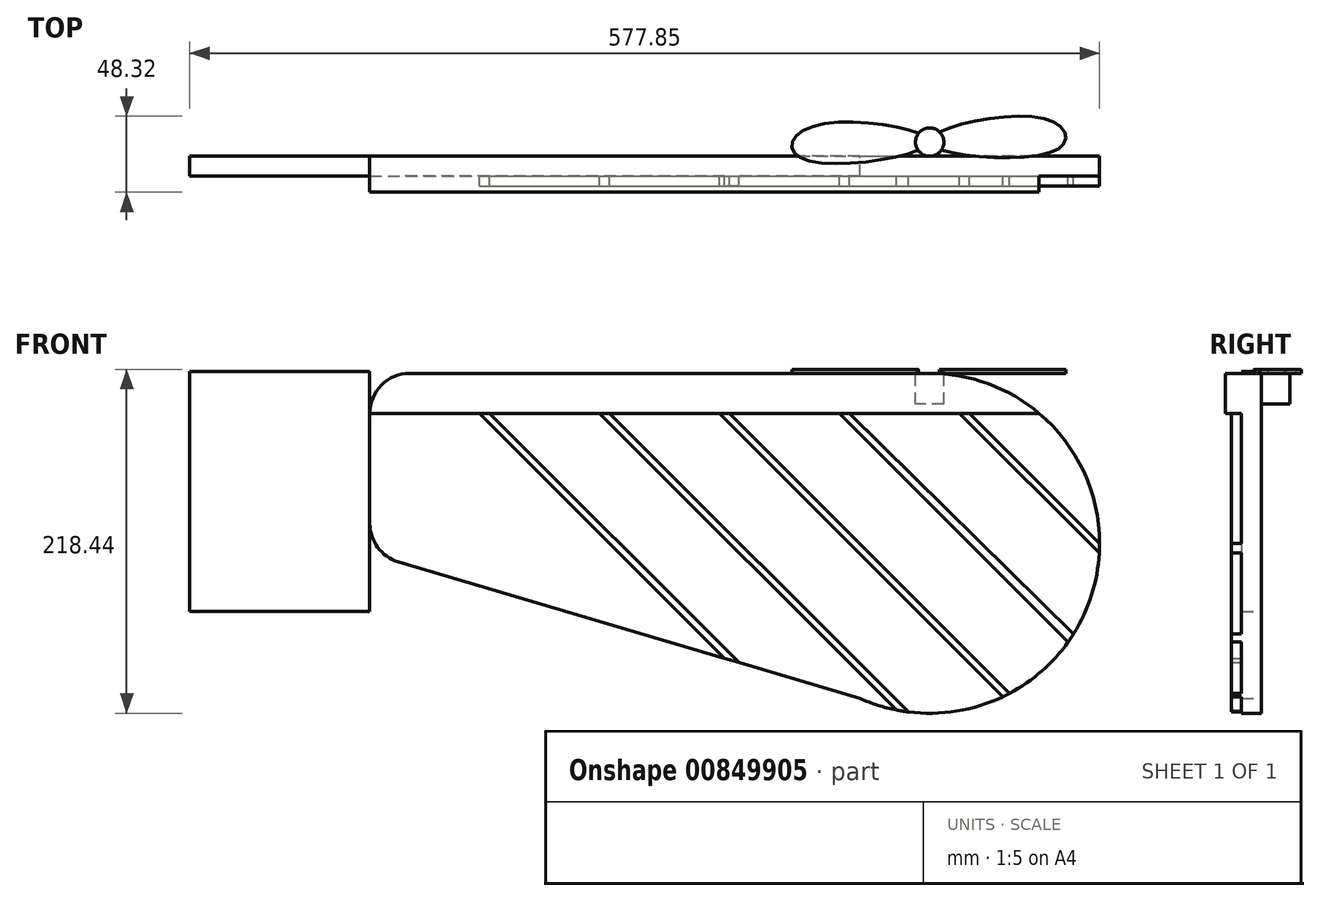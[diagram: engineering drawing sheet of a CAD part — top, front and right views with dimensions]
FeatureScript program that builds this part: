
annotation { "Feature Type Name" : "Feature", "Feature Type Description" : "" }
export const myFeature = defineFeature(function(context is Context, id is Id, definition is map)
    precondition{}
    {
        {
            var Q0;
            Q0=qCreatedBy(makeId("Front.planeOp"),FACE);
            var sketch = newSketch(context, id + "F0", { "sketchPlane" : qUnion([Q0])});
            skLineSegment(sketch, "E0", {"start": v(0, 18.97) * mm, "end": v(0, 88.9) * mm});
            skLineSegment(sketch, "E1", {"start": v(25.4, 114.3) * mm, "end": v(355.6, 114.3) * mm});
            skLineSegment(sketch, "E2", {"start": v(311.37, -92.12) * mm, "end": v(18.2, -5.38) * mm});
            skArc(sketch, "E3", {"start": v(311.37, -92.12) * mm, "mid": v(461.15, -16.27) * mm, "end": v(355.6, 114.3) * mm});
            skPoint(sketch, "E4.visualSharp", {"position": v(0, 114.3) * mm});
            skArc(sketch, "E4.filletArc", {"start": v(25.4, 114.3) * mm, "mid": v(7.44, 106.86) * mm, "end": v(0, 88.9) * mm});
            skPoint(sketch, "E5.visualSharp", {"position": v(0, 0) * mm});
            skArc(sketch, "E5.filletArc", {"start": v(0, 18.97) * mm, "mid": v(5.05, 3.77) * mm, "end": v(18.2, -5.38) * mm});
            skSolve(sketch);
        }
        {
            var Q0;
            Q0=makeQuery(id+"F0.imprint","IMPRINT",FACE,{"disambiguationData":[TD([[makeQuery(id+"F0.imprint","IMPRINT",EDGE,{"derivedFrom":sQuery(id+"F0.wireOp",EDGE,"E0")}),-1.0]])]});
            extrude(context, id + "F1", {"entities" : qUnion([Q0]), "depth" : 12.7 * mm, "offsetDistance" : 25.4 * mm});
        }
        {
            var Q0;
            Q0=makeQuery(id+"F1.opExtrude","CAP_FACE",FACE,{"disambiguationData":[OSD([sQuery(id+"F0.wireOp",EDGE,"E0"),sQuery(id+"F0.wireOp",EDGE,"E1"),sQuery(id+"F0.wireOp",EDGE,"E2"),sQuery(id+"F0.wireOp",EDGE,"E3"),sQuery(id+"F0.wireOp",EDGE,"E4.filletArc"),sQuery(id+"F0.wireOp",EDGE,"E5.filletArc")])],"isStart":false});
            var sketch = newSketch(context, id + "F2", { "sketchPlane" : qUnion([Q0])});
            skLineSegment(sketch, "E6", {"start": v(0, 88.9) * mm, "end": v(425.16, 88.9) * mm});
            skSolve(sketch);
        }
        {
            var Q0;
            {var subQ0=sQuery(id+"F2.wireOp",EDGE,"E6");Q0=makeQuery(id+"F2.imprint","IMPRINT",FACE,{"disambiguationData":[TD([[makeQuery(id+"F2.imprint","IMPRINT",EDGE,{"derivedFrom":subQ0}),1.0]])]});}
            extrude(context, id + "F3", {"entities" : qUnion([Q0]), "operationType" : NewBodyOperationType.ADD, "depth" : 10.16 * mm, "offsetDistance" : 25.4 * mm});
        }
        {
            var Q0;
            Q0=makeQuery(id+"F1.opExtrude","CAP_FACE",FACE,{"disambiguationData":[OSD([sQuery(id+"F0.wireOp",EDGE,"E0"),sQuery(id+"F0.wireOp",EDGE,"E1"),sQuery(id+"F0.wireOp",EDGE,"E2"),sQuery(id+"F0.wireOp",EDGE,"E3"),sQuery(id+"F0.wireOp",EDGE,"E4.filletArc"),sQuery(id+"F0.wireOp",EDGE,"E5.filletArc")])],"isStart":false});
            var sketch = newSketch(context, id + "F4", { "sketchPlane" : qUnion([Q0])});
            skPoint(sketch, "E7", {"position": v(0, 88.9) * mm});
            skPoint(sketch, "E8", {"position": v(69.85, 88.9) * mm});
            skPoint(sketch, "E9", {"position": v(76.2, 88.9) * mm});
            skPoint(sketch, "E10", {"position": v(146.05, 88.9) * mm});
            skPoint(sketch, "E11", {"position": v(152.4, 88.9) * mm});
            skPoint(sketch, "E12", {"position": v(222.25, 88.9) * mm});
            skPoint(sketch, "E13", {"position": v(228.6, 88.9) * mm});
            skPoint(sketch, "E14", {"position": v(298.45, 88.9) * mm});
            skPoint(sketch, "E15", {"position": v(304.8, 88.9) * mm});
            skPoint(sketch, "E16", {"position": v(374.65, 88.9) * mm});
            skPoint(sketch, "E17", {"position": v(381, 88.9) * mm});
            skLineSegment(sketch, "E18", {"start": v(69.85, 88.9) * mm, "end": v(225.45, -66.7) * mm});
            skLineSegment(sketch, "E19", {"start": v(76.2, 88.9) * mm, "end": v(234.47, -69.37) * mm});
            skLineSegment(sketch, "E20", {"start": v(146.05, 88.9) * mm, "end": v(334.46, -99.5) * mm});
            skLineSegment(sketch, "E21", {"start": v(152.4, 88.9) * mm, "end": v(342.05, -100.75) * mm});
            skLineSegment(sketch, "E22", {"start": v(222.25, 88.9) * mm, "end": v(402.18, -91.03) * mm});
            skLineSegment(sketch, "E23", {"start": v(228.6, 88.9) * mm, "end": v(408.53, -91.03) * mm});
            skLineSegment(sketch, "E24", {"start": v(298.45, 88.9) * mm, "end": v(443.57, -56.22) * mm});
            skLineSegment(sketch, "E25", {"start": v(304.8, 88.9) * mm, "end": v(447, -51.1) * mm});
            skLineSegment(sketch, "E26", {"start": v(374.65, 88.9) * mm, "end": v(463.37, 0.18) * mm});
            skLineSegment(sketch, "E27", {"start": v(381, 88.9) * mm, "end": v(463.55, 6.35) * mm});
            skLineSegment(sketch, "E28", {"start": v(69.85, 88.9) * mm, "end": v(76.2, 88.9) * mm});
            skLineSegment(sketch, "E29", {"start": v(225.45, -66.7) * mm, "end": v(234.47, -69.37) * mm});
            skSolve(sketch);
        }
        {
            var Q0;
            Q0=makeQuery(id+"F4.imprint","IMPRINT",FACE,{"disambiguationData":[TD([[makeQuery(id+"F4.imprint","IMPRINT",EDGE,{"derivedFrom":sQuery(id+"F4.wireOp",EDGE,"E18")}),1.0]])]});
            var Q1;
            {var subQ0=sQuery(id+"F4.wireOp",EDGE,"E20");Q1=makeQuery(id+"F4.imprint","IMPRINT",FACE,{"disambiguationData":[TD([[makeQuery(id+"F4.imprint","IMPRINT",EDGE,{"derivedFrom":subQ0}),1.0]])]});}
            var Q2;
            {var subQ0=sQuery(id+"F4.wireOp",EDGE,"E22");Q2=makeQuery(id+"F4.imprint","IMPRINT",FACE,{"disambiguationData":[TD([[makeQuery(id+"F4.imprint","IMPRINT",EDGE,{"derivedFrom":subQ0}),1.0]])]});}
            var Q3;
            {var subQ0=sQuery(id+"F4.wireOp",EDGE,"E24");Q3=makeQuery(id+"F4.imprint","IMPRINT",FACE,{"disambiguationData":[TD([[makeQuery(id+"F4.imprint","IMPRINT",EDGE,{"derivedFrom":subQ0}),1.0]])]});}
            var Q4;
            {var subQ0=sQuery(id+"F4.wireOp",EDGE,"E26");Q4=makeQuery(id+"F4.imprint","IMPRINT",FACE,{"disambiguationData":[TD([[makeQuery(id+"F4.imprint","IMPRINT",EDGE,{"derivedFrom":subQ0}),1.0]])]});}
            extrude(context, id + "F5", {"entities" : qUnion([Q0, Q1, Q2, Q3, Q4]), "operationType" : NewBodyOperationType.ADD, "depth" : 6.35 * mm, "offsetDistance" : 25.4 * mm});
        }
        {
            var Q0;
            Q0=makeQuery(id+"F1.opExtrude","SWEPT_BODY",BODY,{"disambiguationData":[OSD([sQuery(id+"F0.wireOp",EDGE,"E0"),sQuery(id+"F0.wireOp",EDGE,"E1"),sQuery(id+"F0.wireOp",EDGE,"E2"),sQuery(id+"F0.wireOp",EDGE,"E3"),sQuery(id+"F0.wireOp",EDGE,"E4.filletArc"),sQuery(id+"F0.wireOp",EDGE,"E5.filletArc")])]});
            transform(context, id + "F6", {"entities" : qUnion([Q0]), "transformType" : TransformType.TRANSLATION_3D, "dx" : 0 * mm, "dy" : 0 * mm, "dz" : 0 * mm, "makeCopy" : true});
        }
        {
            var Q0;
            Q0=qCreatedBy(makeId("Front.planeOp"),FACE);
            var sketch = newSketch(context, id + "F7", { "sketchPlane" : qUnion([Q0])});
            skLineSegment(sketch, "E30.bottom", {"start": v(0, -36.94) * mm, "end": v(-114.3, -36.94) * mm});
            skLineSegment(sketch, "E30.top", {"start": v(0, 115.46) * mm, "end": v(-114.3, 115.46) * mm});
            skLineSegment(sketch, "E30.left", {"start": v(0, -36.94) * mm, "end": v(0, 115.46) * mm});
            skLineSegment(sketch, "E30.right", {"start": v(-114.3, -36.94) * mm, "end": v(-114.3, 115.46) * mm});
            skSolve(sketch);
        }
        {
            var Q0;
            Q0=makeQuery(id+"F7.imprint","IMPRINT",FACE,{"disambiguationData":[TD([[makeQuery(id+"F7.imprint","IMPRINT",EDGE,{"derivedFrom":sQuery(id+"F7.wireOp",EDGE,"E30.bottom")}),-1.0]])]});
            extrude(context, id + "F8", {"entities" : qUnion([Q0]), "depth" : 12.7 * mm, "offsetDistance" : 25.4 * mm});
        }
        {
            var Q0;
            {var subQ0=sQuery(id+"F0.wireOp",EDGE,"E1");Q0=makeQuery(id+"F3.boolean.opBoolean","MERGE",FACE,{"derivedFrom":[makeQuery(id+"F1.opExtrude","SWEPT_FACE",FACE,{"disambiguationData":[OSD([subQ0])]}),makeQuery(id+"F3.opExtrude","SWEPT_FACE",FACE,{"disambiguationData":[OSD([subQ0])]})]});}
            var sketch = newSketch(context, id + "F9", { "sketchPlane" : qUnion([Q0])});
            skCircle(sketch, "E31", {"center": v(355.63, 9.02) * mm, "radius": 9.02 * mm});
            skPoint(sketch, "E31.first.point", {"position": v(355.6, 0) * mm});
            skPoint(sketch, "E31.second.point", {"position": v(355.6, 18.03) * mm});
            skPoint(sketch, "E31.third.point", {"position": v(346.75, 7.48) * mm});
            skSolve(sketch);
        }
        {
            var Q0;
            Q0=makeQuery(id+"F9.imprint","IMPRINT",FACE,{"disambiguationData":[TD([[makeQuery(id+"F9.imprint","IMPRINT",EDGE,{"derivedFrom":sQuery(id+"F9.wireOp",EDGE,"E31")}),1.0]])]});
            extrude(context, id + "F10", {"entities" : qUnion([Q0]), "oppositeDirection" : true, "depth" : 19.56 * mm, "offsetDistance" : 25.4 * mm});
        }
        {
            var Q0;
            Q0=makeQuery(id+"F10.opExtrude","CAP_FACE",FACE,{"disambiguationData":[OSD([sQuery(id+"F9.wireOp",EDGE,"E31")])],"isStart":true});
            var sketch = newSketch(context, id + "F11", { "sketchPlane" : qUnion([Q0])});
            skFitSpline(sketch, "E32", {"points": [v(355.63, 9.02) * mm, v(431.34, 23.04) * mm, v(437.62, 4.97) * mm, v(355.63, 9.02) * mm]});
            skLineSegment(sketch, "E33", {"start": v(354.34, 30.9) * mm, "end": v(355.63, -7.2) * mm, "construction": true});
            skFitSpline(sketch, "E34.MirrorC", {"points": [v(354.53, 8.98) * mm, v(278.06, 17.83) * mm, v(273.01, -0.62) * mm, v(354.53, 8.98) * mm]});
            skSolve(sketch);
        }
        {
            var Q0;
            {var subQ0=sQuery(id+"F11.wireOp",EDGE,"E34.MirrorC");var subQ1=makeQuery(id+"F10.opExtrude","CAP_EDGE",EDGE,{"disambiguationData":[OSD([sQuery(id+"F9.wireOp",EDGE,"E31")])],"isStart":true});var subQ2=makeQuery(id+"F11.imprint","INTERSECT",VERTEX,{"disambiguationData":[OD(0.0)],"derivedFrom":[subQ1,subQ0]});Q0=makeQuery(id+"F11.imprint","IMPRINT",FACE,{"disambiguationData":[TD([[makeQuery(id+"F11.imprint","IMPRINT",EDGE,{"disambiguationData":[TD([[subQ2,1.0]])],"derivedFrom":subQ0}),1.0]])]});}
            var Q1;
            {var subQ0=sQuery(id+"F11.wireOp",EDGE,"E32");var subQ1=makeQuery(id+"F10.opExtrude","CAP_EDGE",EDGE,{"disambiguationData":[OSD([sQuery(id+"F9.wireOp",EDGE,"E31")])],"isStart":true});var subQ2=makeQuery(id+"F11.imprint","INTERSECT",VERTEX,{"disambiguationData":[OD(0.0)],"derivedFrom":[subQ1,subQ0]});Q1=makeQuery(id+"F11.imprint","IMPRINT",FACE,{"disambiguationData":[TD([[makeQuery(id+"F11.imprint","IMPRINT",EDGE,{"disambiguationData":[TD([[subQ2,1.0]])],"derivedFrom":subQ0}),-1.0]])]});}
            extrude(context, id + "F12", {"entities" : qUnion([Q0, Q1]), "depth" : 2.54 * mm, "offsetDistance" : 25.4 * mm});
        }
    });
